# Revit family: IS_TonicII_RV056__BIM_FR
name_source: partatom
category: Plumbing Fixtures
revit_build: Autodesk Revit 2017 (Build: 20160225_1515(x64)
units: mm (PartAtom-declared; Revit-internal decimal feet)

## family parameters
Always vertical = No
Cut with Voids When Loaded = No
OmniClass Number = 23.45.05.14.21.11
OmniClass Title = Bath/Shower Units
Part Type = Normal
Room Calculation Point = No
Round Connector Dimension = Use Diameter
Shared = No
Work Plane-Based = No

## types (1)
- RV05667 - TONIC II BOITE TRANSPARENTE
    Accessoires = www.idealspec.fr
    Auteur = Ideal Standard
    BOSUseNativeGeometries = 1
    Bim-NomDuProjet = ISI_IdealStandard_BathroomIntegratedFurniture_TonicII_RV056_
    CodeBarre = 3391500569478
    Conformité = NF
    ConseilsDInstallation = 0
    Cost = 0 $
    Couleur = Naturel
    CoûtDeRemplacement = 0
    DateDeCréation = 2018_08_03
    Dimensions = 71 x 100 x 100mm
    EAN code = https://3391500569478
    Espace = Interne
    Finition = Naturel
    Forme = rectangulaire
    Hauteur = 71 mm
    IfcExportAs = Bathroom integrated furniture
    IfcExportType = IfcFurnitureType
    InformationsProduit = www.idealspec.fr
    Largeur = 100 mm  [stored 0.328084 ft]
    Longueur = 100 mm  [stored 0.328084 ft]
    Marque = Ideal Standard
    Model = RV05667
    Nom = BathroomIntegratedFurniture_TonicII_RV056__IdealStandard
    PoidsNet = 1,00 KG
    Profondeur = 0 mm  [stored 0 ft]
    Raccordement = Plomberie
    Révision = 1
    URL = www.idealspec.fr
    Uniclass2015Code = Pr_40_30_78_05
    Uniclass2015Title = Bathroom integrated furniture
    Uniclass2015Version = Products v1.1
    UnitéDeMesure = Millimètres
    UnitéDeTemps = An
    UnitéMonétaire = €
    UrlDuFabricant = www.idealspec.fr
    Version = 1

note: [stored X ft] marks values corroborated as IEEE doubles in the binary element streams (Revit-internal decimal feet)

## geometry (parser evidence)
native form markers: Sweep x3
no freeform markers — native parametric forms only
